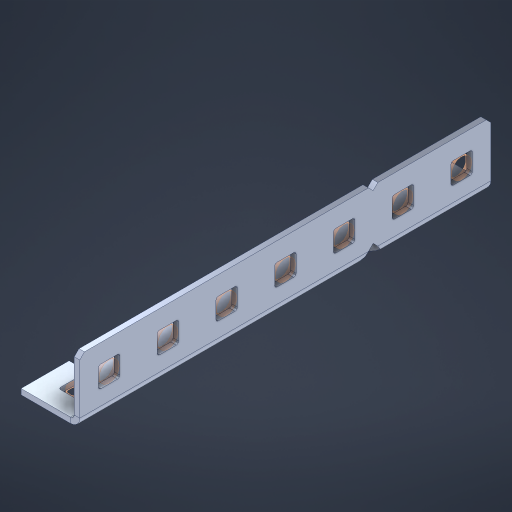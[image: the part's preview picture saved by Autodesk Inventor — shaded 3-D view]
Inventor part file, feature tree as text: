
AUTODESK INVENTOR PART (.ipt)
format: ipt  version: 2023 (Build 270158000, 158)  size: 603,136 bytes
history: native  units: in
note: dims shown in document units (in); Inventor stores cm internally (conversion verified against a paired STEP export)
features: other x28, extrude x19, sheet_metal_op x11, sketch x10, pattern_linear x2, mirror x1, chamfer x1
ambient origin geometry x8: Origin, YZ Plane, XZ Plane, XY Plane, X Axis, Y Axis, Z Axis, Center Point
bodies: Solid1 (feature_tree), Body (feature_tree)
feature tree (72):
  sheet_metal_op  "Flanges"
  other  "Flange Pattern Plane"
  other  "Flange Pattern Sketch"
  sheet_metal_op  "Flange Pattern"
  sheet_metal_op  "Body Pattern"
  pattern_linear  "Center Pattern"  Spacing1=0.0469in  [1 undecoded]
  other  "Arc Length"
  mirror  "Notch Mirror"
  pattern_linear  "Notch Pattern"  Spacing1=0.182in  [1 undecoded]
  chamfer  "End Chamfer"
  extrude  "Half Cut"  Depth=0.02in
  sketch  "Sketch1"  dims[d0=1.0in]
  other  "Plate1"
  sketch  "Sketch2"  dims[d1=3.5in]
  other  "Plate2"
  sheet_metal_op  "Bend1"
  sheet_metal_op  "Corner1"
  sketch  "Sketch3"  dims[d2=0.0469in]
  sketch  "Sketch7"  dims[d3=0.0469in]
  other  "Srf1"
  other  "Srf2"
  sketch  "Sketch8"  dims[d4=0.0234in]
  sketch  "Sketch9"  dims[d5=0.0938in]
  other  "Srf91"
  sheet_metal_op  "Body Pattern Sketch"
  other  "Srf92"
  sketch  "Sketch13"  dims[d6=0.0469in]
  sketch  "Sketch14"  dims[d7=0.5in d8=90.0deg d9=0.0312in]
  sketch  "Sketch15"  dims[d10=0.1875in]
  sketch  "Sketch16"  dims[d11=0.0469in d12=0.0469in d16=0.182in d17=0.02in d18=0.0469in d19=0.0in d20=0.25in d21=0.25in d38=2.7559in d40=0.5in d41=0.3937in d43=1.0in d46=0.172in d47=1.0in d48=0.0in d49=0.182in d50=0.02in d51=0.25in d52=0.25in d53=0.0469in d54=0.0in d55=0.172in d56=1.0in d57=0.0in d58=0.25in d60=2.7559in d62=0.5in d63=0.3937in d65=0.5in d85=0.1227in d86=0.1659in d88=0.04in d89=0.0469in d90=0.0in d91=0.04in d92=0.0491in d95=2.5in d96=0.04in d97=0.25in d98=45.0deg d99=0.25in d100=0.5in d101=0.0in d102=2.497in d106=0.182in d107=0.02in d108=0.5in d109=0.5in d110=0.0469in d111=0.0in d112=0.172in d113=0.5in d114=0.0in d117=0.5in d118=0.5in d119=0.5in]
  other  "Srf786"
  other  "Srf823"
  other  "Srf824"
  other  "Srf825"
  other  "Srf826"
  other  "Srf827"
  other  "Srf856"
  other  "Srf857"
  other  "Srf858"
  other  "Srf859"
  other  "Srf860"
  other  "Srf889"
  other  "Srf890"
  other  "Srf891"
  other  "Srf892"
  other  "Srf893"
  other  "Srf894"
  sheet_metal_op  "Flange Stamp"
  sheet_metal_op  "Flange Circle"
  sheet_metal_op  "Body Stamp"
  sheet_metal_op  "Body Circle"
  other  "Center Stamp"
  other  "Center Circle"
  sheet_metal_op  "Notch"
  extrude  "ExtrusionSrf2"  Depth=0.0469in
  extrude  "ExtrusionSrf92"  TaperAngle=0.0deg  [1 undecoded]
  extrude  "ExtrusionSrf823"  Depth=0.5in
  extrude  "ExtrusionSrf824"  Depth=0.5in
  extrude  "ExtrusionSrf825"  Depth=0.5in
  extrude  "ExtrusionSrf826"  Depth=0.5in
  extrude  "ExtrusionSrf827"  Depth=1.0in TaperAngle=0.0deg
  extrude  "ExtrusionSrf856"  Depth=0.182in
  extrude  "ExtrusionSrf857"  Depth=0.02in
  extrude  "ExtrusionSrf858"  Depth=0.5in
  extrude  "ExtrusionSrf859"  Depth=0.5in
  extrude  "ExtrusionSrf860"  Depth=0.0469in
  extrude  "ExtrusionSrf889"  TaperAngle=0.0deg  [1 undecoded]
  extrude  "ExtrusionSrf890"  Depth=0.5in
  extrude  "ExtrusionSrf891"  Depth=1.0in TaperAngle=0.0deg
  extrude  "ExtrusionSrf892"  Depth=0.5in
  extrude  "ExtrusionSrf893"  Depth=0.5in
  extrude  "ExtrusionSrf894"  Depth=0.5in
note: 4 required parameter values undecoded (feature->parameter linkage not recoverable at this tier; creation-order binding heuristic only, values carry confidence <= 0.55)
